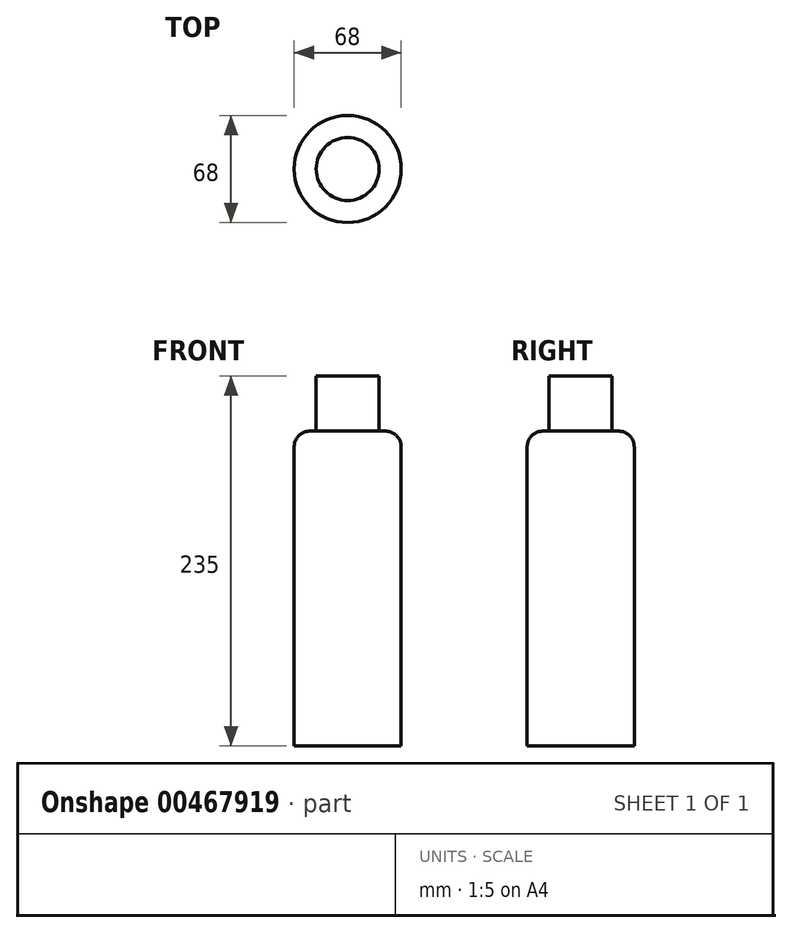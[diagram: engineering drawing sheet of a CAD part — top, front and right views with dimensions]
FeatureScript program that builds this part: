
annotation { "Feature Type Name" : "Feature", "Feature Type Description" : "" }
export const myFeature = defineFeature(function(context is Context, id is Id, definition is map)
    precondition{}
    {
        {
            var Q0;
            Q0=qCreatedBy(makeId("Front.planeOp"),FACE);
            var sketch = newSketch(context, id + "F0", { "sketchPlane" : qUnion([Q0])});
            skLineSegment(sketch, "E0", {"start": v(0, 147.48) * mm, "end": v(0, -17.4) * mm, "construction": true});
            skLineSegment(sketch, "E1", {"start": v(0, 0) * mm, "end": v(-34, 0) * mm});
            skLineSegment(sketch, "E2", {"start": v(-34, 0) * mm, "end": v(-34, 190) * mm});
            skPoint(sketch, "E3.visualSharp", {"position": v(-34, 106.95) * mm});
            skArc(sketch, "E3.filletArc", {"start": v(-24, 200) * mm, "mid": v(-31.07, 197.07) * mm, "end": v(-34, 190) * mm});
            skLineSegment(sketch, "E4", {"start": v(-24, 200) * mm, "end": v(-20, 200) * mm});
            skLineSegment(sketch, "E5", {"start": v(-20, 200) * mm, "end": v(-20, 235) * mm});
            skLineSegment(sketch, "E6", {"start": v(-20, 235) * mm, "end": v(0, 235) * mm});
            skLineSegment(sketch, "E7", {"start": v(0, 235) * mm, "end": v(0, 0) * mm});
            skSolve(sketch);
        }
        {
            var Q0;
            Q0 = qSketchRegion(id + "F0", true);
            var Q1;
            Q1=sQuery(id+"F0.wireOp",EDGE,"E0");
            revolve(context, id + "F1", {"entities" : qUnion([Q0]), "axis" : qUnion([Q1]), "revolveType" : RevolveType.FULL});
        }
    });
